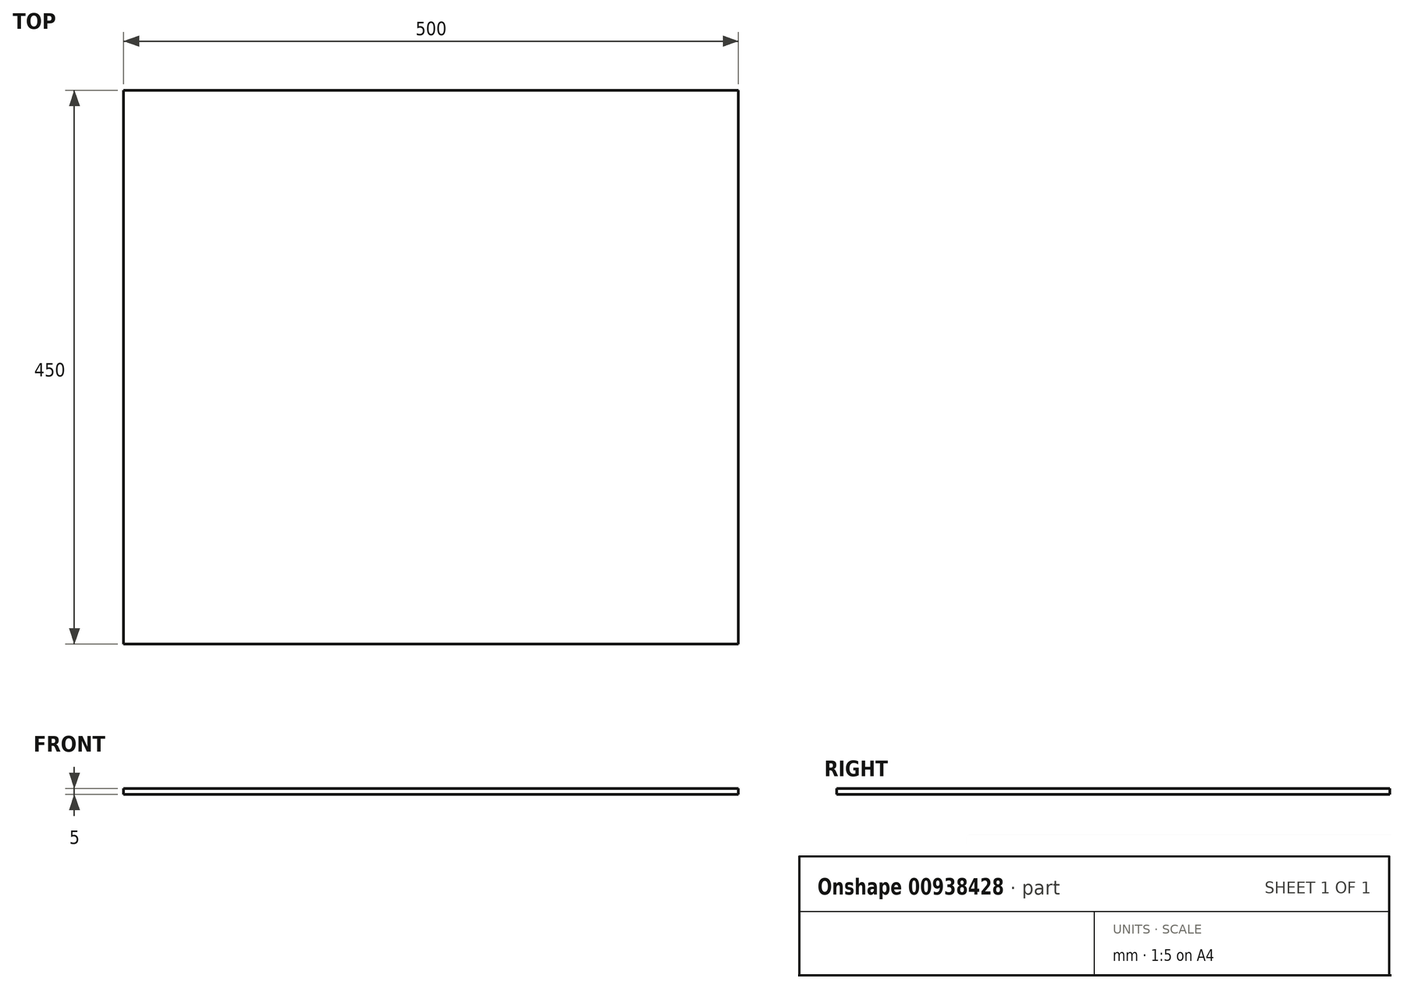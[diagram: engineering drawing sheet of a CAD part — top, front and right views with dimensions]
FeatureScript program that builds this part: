
annotation { "Feature Type Name" : "Feature", "Feature Type Description" : "" }
export const myFeature = defineFeature(function(context is Context, id is Id, definition is map)
    precondition{}
    {
        {
            assignVariable(context, id + "F0", {"name" : "glass_W", "anyValue" : 5});
        }
        {
            var Q0;
            Q0=qCreatedBy(makeId("Top.planeOp"),FACE);
            var sketch = newSketch(context, id + "F1", { "sketchPlane" : qUnion([Q0])});
            skLineSegment(sketch, "E0.bottom", {"start": v(-250, 225) * mm, "end": v(250, 225) * mm});
            skLineSegment(sketch, "E0.top", {"start": v(-250, -225) * mm, "end": v(250, -225) * mm});
            skLineSegment(sketch, "E0.left", {"start": v(-250, 225) * mm, "end": v(-250, -225) * mm});
            skLineSegment(sketch, "E0.right", {"start": v(250, 225) * mm, "end": v(250, -225) * mm});
            skPoint(sketch, "E0.middle", {"position": v(0, 0) * mm});
            skSolve(sketch);
        }
        {
            var Q0;
            Q0=makeQuery(id+"F1.imprint","IMPRINT",FACE,{"disambiguationData":[TD([[makeQuery(id+"F1.imprint","IMPRINT",EDGE,{"derivedFrom":sQuery(id+"F1.wireOp",EDGE,"E0.bottom")}),-1.0]])]});
            extrude(context, id + "F2", {"entities" : qUnion([Q0]), "depth" : (getVariable(context, 'glass_W')) * mm, "offsetDistance" : 25 * mm});
        }
    });
